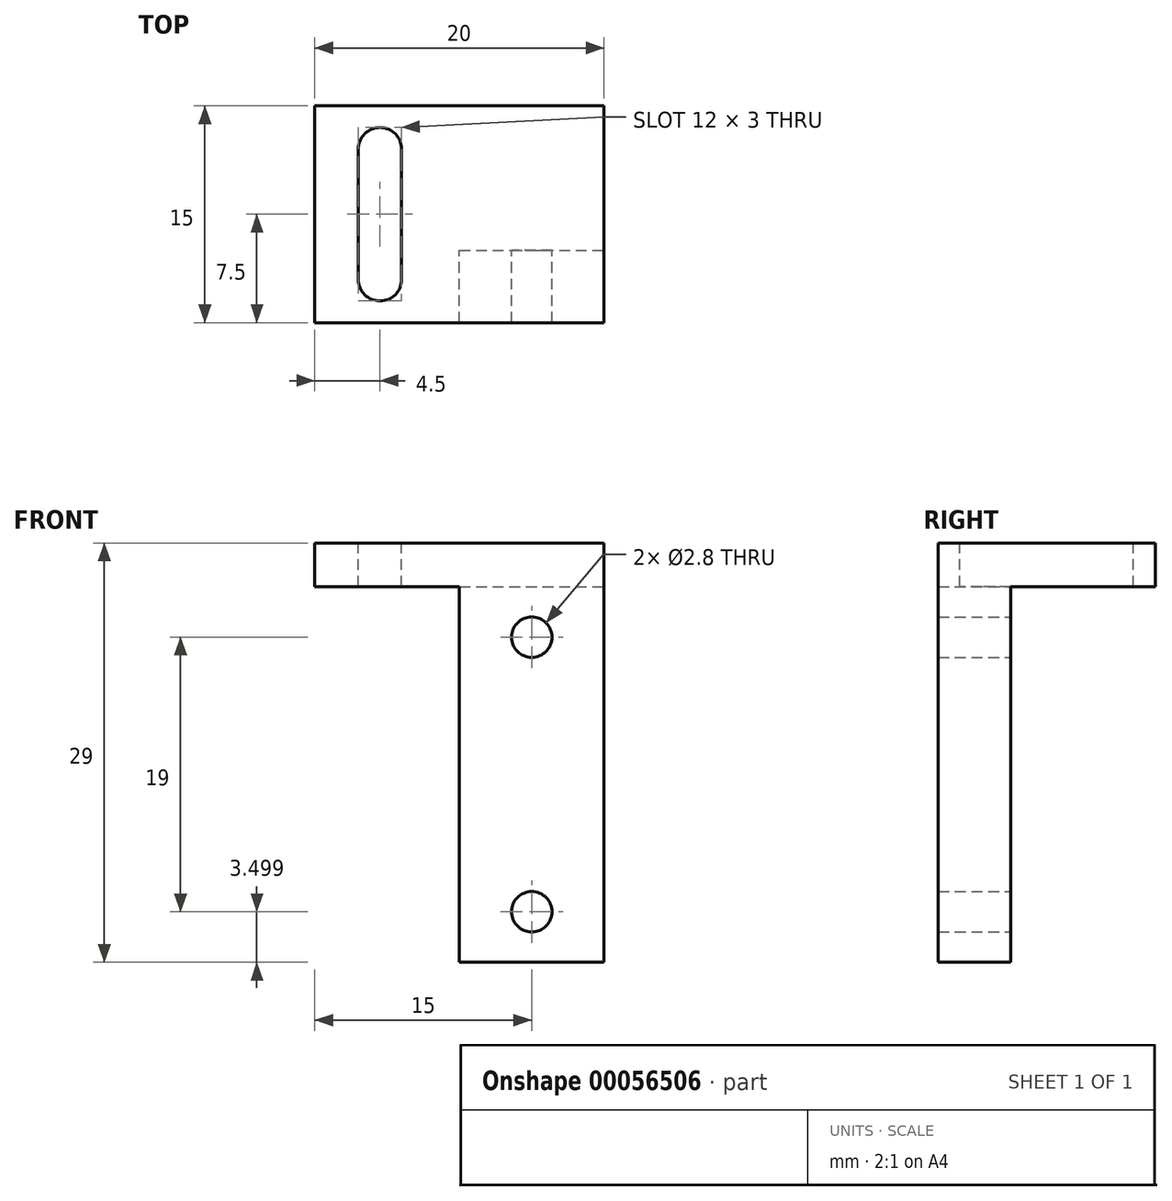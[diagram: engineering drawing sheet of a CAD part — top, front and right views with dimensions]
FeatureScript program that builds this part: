
annotation { "Feature Type Name" : "Feature", "Feature Type Description" : "" }
export const myFeature = defineFeature(function(context is Context, id is Id, definition is map)
    precondition{}
    {
        {
            var Q0;
            Q0=qCreatedBy(makeId("Front.planeOp"),FACE);
            var sketch = newSketch(context, id + "F0", { "sketchPlane" : qUnion([Q0])});
            skLineSegment(sketch, "E0.bottom", {"start": v(-2.41, 8.63) * mm, "end": v(7.59, 8.63) * mm});
            skLineSegment(sketch, "E0.top", {"start": v(-2.41, -20.37) * mm, "end": v(7.59, -20.37) * mm});
            skLineSegment(sketch, "E0.left", {"start": v(-2.41, 8.63) * mm, "end": v(-2.41, -20.37) * mm});
            skLineSegment(sketch, "E0.right", {"start": v(7.59, 8.63) * mm, "end": v(7.59, -20.37) * mm});
            skLineSegment(sketch, "E1.0", {"start": v(-2.41, 5.63) * mm, "end": v(5.59, 5.63) * mm, "construction": true});
            skSolve(sketch);
        }
        {
            var Q0;
            Q0=makeQuery(id+"F0.imprint","IMPRINT",FACE,{"disambiguationData":[TD([[makeQuery(id+"F0.imprint","IMPRINT",EDGE,{"derivedFrom":sQuery(id+"F0.wireOp",EDGE,"E0.bottom")}),-1.0]])]});
            extrude(context, id + "F1", {"entities" : qUnion([Q0]), "depth" : 5 * mm});
        }
        {
            var Q0;
            Q0=makeQuery(id+"F1.opExtrude","CAP_FACE",FACE,{"disambiguationData":[OSD([sQuery(id+"F0.wireOp",EDGE,"E0.bottom"),sQuery(id+"F0.wireOp",EDGE,"E0.top"),sQuery(id+"F0.wireOp",EDGE,"E0.left"),sQuery(id+"F0.wireOp",EDGE,"E0.right")])],"isStart":true});
            var sketch = newSketch(context, id + "F2", { "sketchPlane" : qUnion([Q0])});
            skLineSegment(sketch, "E2.0", {"start": v(-2.59, 9.63) * mm, "end": v(-2.59, -20.37) * mm, "construction": true});
            skCircle(sketch, "E3", {"center": v(-2.59, 2.13) * mm, "radius": 1.4 * mm});
            skCircle(sketch, "E4", {"center": v(-2.59, -16.87) * mm, "radius": 1.4 * mm});
            skLineSegment(sketch, "E5.0", {"start": v(2.41, -16.87) * mm, "end": v(-7.59, -16.87) * mm, "construction": true});
            skLineSegment(sketch, "E6.0", {"start": v(2.41, 2.13) * mm, "end": v(-7.59, 2.13) * mm, "construction": true});
            skSolve(sketch);
        }
        {
            var Q0;
            Q0=qSketchRegion(id+"F2",true);
            extrude(context, id + "F3", {"entities" : qUnion([Q0]), "operationType" : NewBodyOperationType.REMOVE, "oppositeDirection" : true, "depth" : 25 * mm});
        }
        {
            var Q0;
            Q0=makeQuery(id+"F1.opExtrude","SWEPT_FACE",FACE,{"disambiguationData":[OSD([sQuery(id+"F0.wireOp",EDGE,"E0.left")])]});
            var sketch = newSketch(context, id + "F4", { "sketchPlane" : qUnion([Q0])});
            skLineSegment(sketch, "E7.0", {"start": v(5, 5.63) * mm, "end": v(0, 5.63) * mm});
            skSolve(sketch);
        }
        {
            var Q0;
            Q0=qSketchRegion(id+"F4",true);
            var Q1;
            {var subQ2=sQuery(id+"F4.wireOp",EDGE,"E7.0");Q1=makeQuery(id+"F4.imprint","IMPRINT",FACE,{"disambiguationData":[TD([[makeQuery(id+"F4.imprint","IMPRINT",EDGE,{"derivedFrom":subQ2}),-1.0]])]});}
            extrude(context, id + "F5", {"entities" : qUnion([Q0, Q1]), "operationType" : NewBodyOperationType.ADD, "depth" : 10 * mm});
        }
        {
            var Q0;
            {var subQ0=sQuery(id+"F0.wireOp",EDGE,"E0.bottom");var subQ1=sQuery(id+"F0.wireOp",EDGE,"E0.left");var subQ2=makeQuery(id+"F1.opExtrude","CAP_EDGE",EDGE,{"disambiguationData":[OSD([subQ1])],"isStart":false});Q0=makeQuery(id+"F5.boolean.opBoolean","MERGE",FACE,{"derivedFrom":[makeQuery(id+"F1.opExtrude","CAP_FACE",FACE,{"disambiguationData":[OSD([subQ0,sQuery(id+"F0.wireOp",EDGE,"E0.top"),subQ1,sQuery(id+"F0.wireOp",EDGE,"E0.right")])],"isStart":false}),makeQuery(id+"F5.opExtrude","SWEPT_FACE",FACE,{"disambiguationData":[OSD([subQ1]),TDD([makeQuery(id+"F4.imprint","IMPRINT",EDGE,{"disambiguationData":[TD([[makeQuery(id+"F4.imprint","INTERSECT",VERTEX,{"derivedFrom":[subQ2,sQuery(id+"F4.wireOp",EDGE,"E7.0")]}),1.0]])],"derivedFrom":subQ2})])]})]});}
            var sketch = newSketch(context, id + "F6", { "sketchPlane" : qUnion([Q0])});
            skLineSegment(sketch, "E8", {"start": v(-2.41, 5.63) * mm, "end": v(7.59, 5.63) * mm});
            skSolve(sketch);
        }
        {
            var Q0;
            {var subQ1=sQuery(id+"F6.wireOp",EDGE,"E8");Q0=makeQuery(id+"F6.imprint","IMPRINT",FACE,{"disambiguationData":[TD([[makeQuery(id+"F6.imprint","IMPRINT",EDGE,{"derivedFrom":subQ1}),1.0]])]});}
            extrude(context, id + "F7", {"entities" : qUnion([Q0]), "operationType" : NewBodyOperationType.ADD, "oppositeDirection" : true, "depth" : 15 * mm});
        }
        {
            var Q0;
            {var subQ0=sQuery(id+"F0.wireOp",EDGE,"E0.bottom");var subQ1=sQuery(id+"F0.wireOp",EDGE,"E0.left");Q0=makeQuery(id+"F7.boolean.opBoolean","MERGE",FACE,{"derivedFrom":[makeQuery(id+"F5.boolean.opBoolean","MERGE",FACE,{"derivedFrom":[makeQuery(id+"F1.opExtrude","SWEPT_FACE",FACE,{"disambiguationData":[OSD([subQ0])]}),makeQuery(id+"F5.opExtrude","SWEPT_FACE",FACE,{"disambiguationData":[OSD([subQ0,subQ1])]})]}),makeQuery(id+"F7.opExtrude","SWEPT_FACE",FACE,{"disambiguationData":[OSD([subQ0,subQ1])]})]});}
            var sketch = newSketch(context, id + "F8", { "sketchPlane" : qUnion([Q0])});
            skLineSegment(sketch, "E9.0", {"start": v(-7.91, -10) * mm, "end": v(-7.91, 13.41) * mm, "construction": true});
            skLineSegment(sketch, "E10.0", {"start": v(-6.41, -2) * mm, "end": v(-6.41, 7) * mm});
            skLineSegment(sketch, "E11.0", {"start": v(-9.41, -2) * mm, "end": v(-9.41, 7) * mm});
            skLineSegment(sketch, "E12.0", {"start": v(-12.41, 7) * mm, "end": v(7.59, 7) * mm, "construction": true});
            skLineSegment(sketch, "E13.0", {"start": v(-12.41, -2) * mm, "end": v(7.59, -2) * mm, "construction": true});
            skArc(sketch, "E14", {"start": v(-9.41, 7) * mm, "mid": v(-7.91, 8.5) * mm, "end": v(-6.41, 7) * mm});
            skArc(sketch, "E15", {"start": v(-6.41, -2) * mm, "mid": v(-7.91, -3.5) * mm, "end": v(-9.41, -2) * mm});
            skSolve(sketch);
        }
        {
            var Q0;
            Q0=makeQuery(id+"F8.imprint","IMPRINT",FACE,{"disambiguationData":[TD([[makeQuery(id+"F8.imprint","IMPRINT",EDGE,{"derivedFrom":sQuery(id+"F8.wireOp",EDGE,"a678a36d-41d2-427d-8e55-0325338021f2.0")}),1.0]])]});
            var Q1;
            Q1=makeQuery(id+"F8.imprint","IMPRINT",FACE,{"disambiguationData":[TD([[makeQuery(id+"F8.imprint","IMPRINT",EDGE,{"derivedFrom":sQuery(id+"F8.wireOp",EDGE,"E10.0")}),1.0]])]});
            var Q2;
            Q2=sQuery(id+"F8.wireOp",EDGE,"a3b55649-b8dd-449b-a23e-8d3800de4019");
            var Q3;
            Q3=sQuery(id+"F8.wireOp",EDGE,"a678a36d-41d2-427d-8e55-0325338021f2.1");
            var Q4;
            Q4=sQuery(id+"F8.wireOp",EDGE,"a678a36d-41d2-427d-8e55-0325338021f2.0");
            var Q5;
            Q5=sQuery(id+"F8.wireOp",EDGE,"b0d7fb9c-0a67-47c0-9b60-9e4a61582d00");
            var Q6;
            Q6=sQuery(id+"F8.wireOp",EDGE,"8b5e1ef5-08ee-4b97-a625-3d02ef5d0c2a.0");
            var Q7;
            Q7=sQuery(id+"F8.wireOp",EDGE,"718d5cb8-3b57-48ea-b748-e179312c4179.0");
            extrude(context, id + "F9", {"entities" : qUnion([Q0, Q1]), "operationType" : NewBodyOperationType.REMOVE, "surfaceEntities" : qUnion([Q2, Q3, Q4, Q5, Q6, Q7]), "oppositeDirection" : true, "depth" : 25 * mm});
        }
    });
